# Revit family: Gira_0282600
name_source: partatom
category: Electrical Fixtures
revit_build: Autodesk Revit 2017 (Build: 20160225_1515(x64)
units: mm (PartAtom-declared; Revit-internal decimal feet)

## family parameters
Cut with Voids When Loaded = No
Host = Face
Maintain Annotation Orientation = No
Part Type = Normal
Room Calculation Point = No
Round Connector Dimension = Use Diameter
Shared = No

## types (1)
- Adapter fr. square 50 x 50 mm System 55 stainl.steel(lac.)
    Available = No
    BIM (1) = https://media.stage.bim.site
    Category = Transition adapter for domestic switching devices
    Colour = Stainless steel
    Data sheet (1) = https://katalog.gira.de
    Default Elevation = 1219 mm
    Description = Adap.fr.square 50x50mm Sys55 SSTl,Adapter frame with square cut-out for devices with cover (50 x 50 mm),,stainless steel (lacquered),Features:,- Devices with a square central plate (50 x 50 mm) from other manufacturers, e. g. Alcatel, AMP Econo Link System, Brand-Rex, BTR, Cellpack ITT Cannon Cat. 5, Deutsche Telekom, Drahtex, Hirose, Kannegieter BICC Brand Rex, Kerpen ELine 600, Krone, Molex, Nedap, Panduit, Quante, Reichle de Massari, Rutenbeck, Schumann Netzwerktechnik, HomeWay, Siemens ICCS 100, 300 and 600, Telegärtner, Telenorma, TKM (4 x RJ45 shielded, Cat. 5) can be integrated into the design line with the adapter frame and cover frame (1-gang to 5-gang).
    Dimensions = SQ50 / SQ50
    GTIN = 4010337022015
    HAN = 0282600
    HeinzeBIM = https://bimportal.heinze.de
    Lockable = No
    Manufacturer = Gira
    Manufacturer URL = https://www.gira.de
    Name = Adapter fr. square 50 x 50 mm System 55 stainl.steel(lac.)
    URL = http://katalog.gira.de
    With hinged lid = No
    With label space = No

## geometry (parser evidence)
native form markers: Sweep x2
no freeform markers — native parametric forms only
